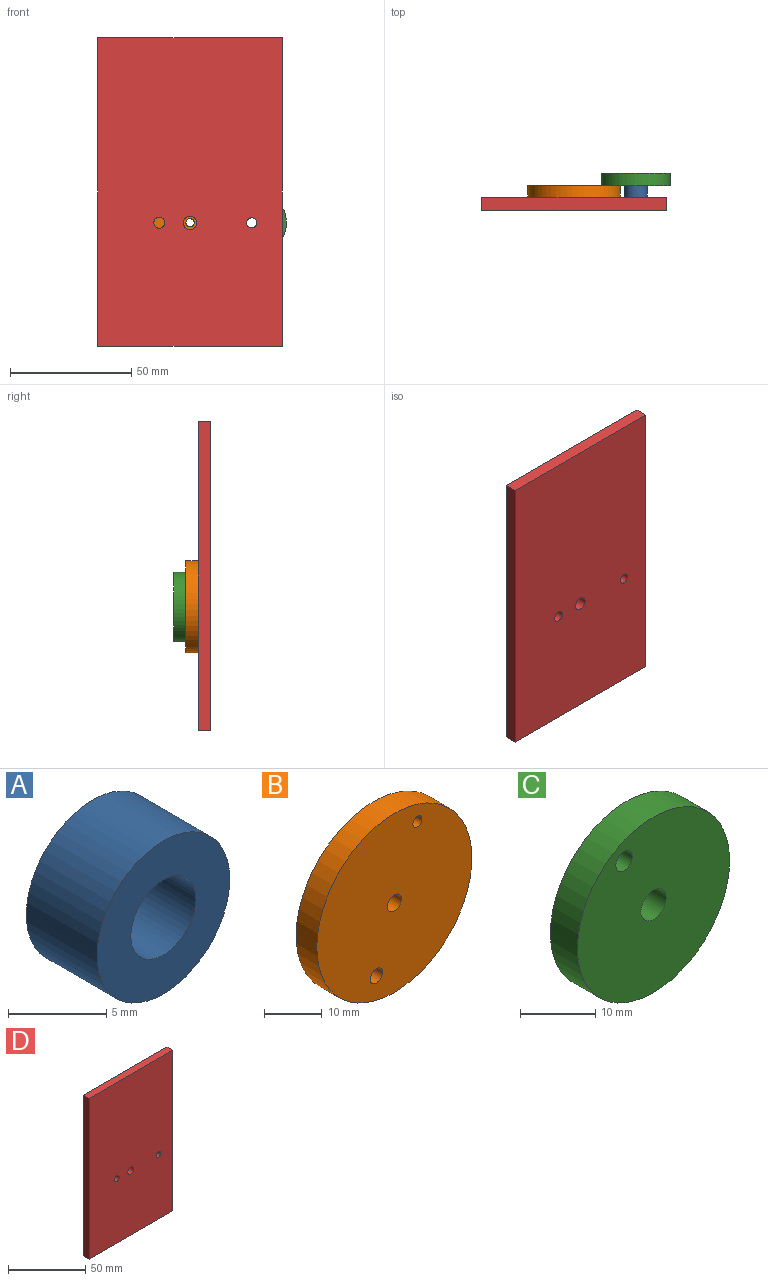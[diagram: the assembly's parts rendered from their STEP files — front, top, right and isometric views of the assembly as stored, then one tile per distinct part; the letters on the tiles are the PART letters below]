
ASSEMBLY  parts=4 mates=5
PART A: 4 faces, bbox 9.5x5.1x9.5 mm
  f0: cylinder r=2.33mm len=5.08mm, axis (0,1,0), area 74.5mm2, adj f2,f3
  f1: cylinder r=4.76mm len=9.53mm, axis (0,1,0), area 152mm2, adj f2,f3
  f2: plane 9.53x9.53mm, normal (0,-1,0), area 54.1mm2, adj f0,f1
  f3: plane 9.53x9.53mm, normal (0,1,0), area 54.1mm2, adj f0,f1
PART B: 6 faces, bbox 38.1x5.1x38.1 mm
  f0: cylinder r=1.71mm len=5.08mm, axis (0,1,0), area 54.6mm2, adj f4,f5
  f1: cylinder r=1.11mm len=5.08mm, axis (0,1,0), area 35.5mm2, adj f4,f5
  f2: cylinder r=1.53mm len=5.08mm, axis (0,1,0), area 48.8mm2, adj f4,f5
  f3: cylinder r=19.05mm len=38.1mm, axis (0,1,0), area 608mm2, adj f4,f5
  f4: plane 38.1x38.1mm, normal (0,-1,0), area 1119.7mm2, adj f0,f1,f2,f3
  f5: plane 38.1x38.1mm, normal (0,1,0), area 1119.7mm2, adj f0,f1,f2,f3
PART C: 5 faces, bbox 28.6x5.1x28.6 mm
  f0: cylinder r=2.37mm len=5.08mm, axis (0,1,0), area 75.5mm2, adj f3,f4
  f1: cylinder r=1.54mm len=5.08mm, axis (0,1,0), area 49.3mm2, adj f3,f4
  f2: cylinder r=14.29mm len=28.58mm, axis (0,1,0), area 456mm2, adj f3,f4
  f3: plane 28.58x28.58mm, normal (0,-1,0), area 616.2mm2, adj f0,f1,f2
  f4: plane 28.58x28.58mm, normal (0,1,0), area 616.2mm2, adj f0,f1,f2
PART D: 9 faces, bbox 76.2x5.1x127 mm
  f0: plane 76.2x5.08mm, normal (0,0,1), area 387.1mm2, adj f1,f6,f7,f8
  f1: plane 127x5.08mm, normal (-1,0,0), area 645.2mm2, adj f0,f2,f7,f8
  f2: plane 76.2x5.08mm, normal (0,0,-1), area 387.1mm2, adj f1,f6,f7,f8
  f3: cylinder r=2.08mm len=5.08mm, axis (0,1,0), area 66.3mm2, adj f7,f8
  f4: cylinder r=2.78mm len=5.57mm, axis (0,1,0), area 88.8mm2, adj f7,f8
  f5: cylinder r=2.25mm len=5.08mm, axis (0,1,0), area 72mm2, adj f7,f8
  f6: plane 127x5.08mm, normal (1,0,0), area 645.2mm2, adj f0,f2,f7,f8
  f7: plane 127x76.2mm, normal (0,-1,0), area 9623.5mm2, adj f0,f1,f2,f3,f4,f5,f6
  f8: plane 127x76.2mm, normal (0,1,0), area 9623.5mm2, adj f0,f1,f2,f3,f4,f5,f6
PLACE A rot(axis=(0,-1,0),3deg) t=(88.81,-34.23,-159.11)mm
PLACE B rot(axis=(0,-1,0),90.4deg) t=(37.27,-34.23,-60.23)mm
PLACE C rot(axis=(-0.69,0,-0.73),180deg) t=(-17.56,-34.23,-60.52)mm
PLACE D t=(0.17,-39.31,-51.42)mm fixed
MATE revolute D.f4 <-> B.f0  axis (0,1,0) through (-0.97,-39.31,-116.76)mm
MATE cylindrical D.f4 <-> B.f0  axis (0,1,0) through (-0.97,-39.31,-116.76)mm
MATE fastened A.f0 <-> C.f0  axis (0,1,0) through (24.43,-34.23,-116.76)mm
MATE revolute A.f0 <-> D.f3  axis (0,-1,0) through (24.43,-39.31,-116.76)mm
MATE cylindrical D.f3 <-> C.f0  axis (0,1,0) through (24.43,-39.31,-116.76)mm
